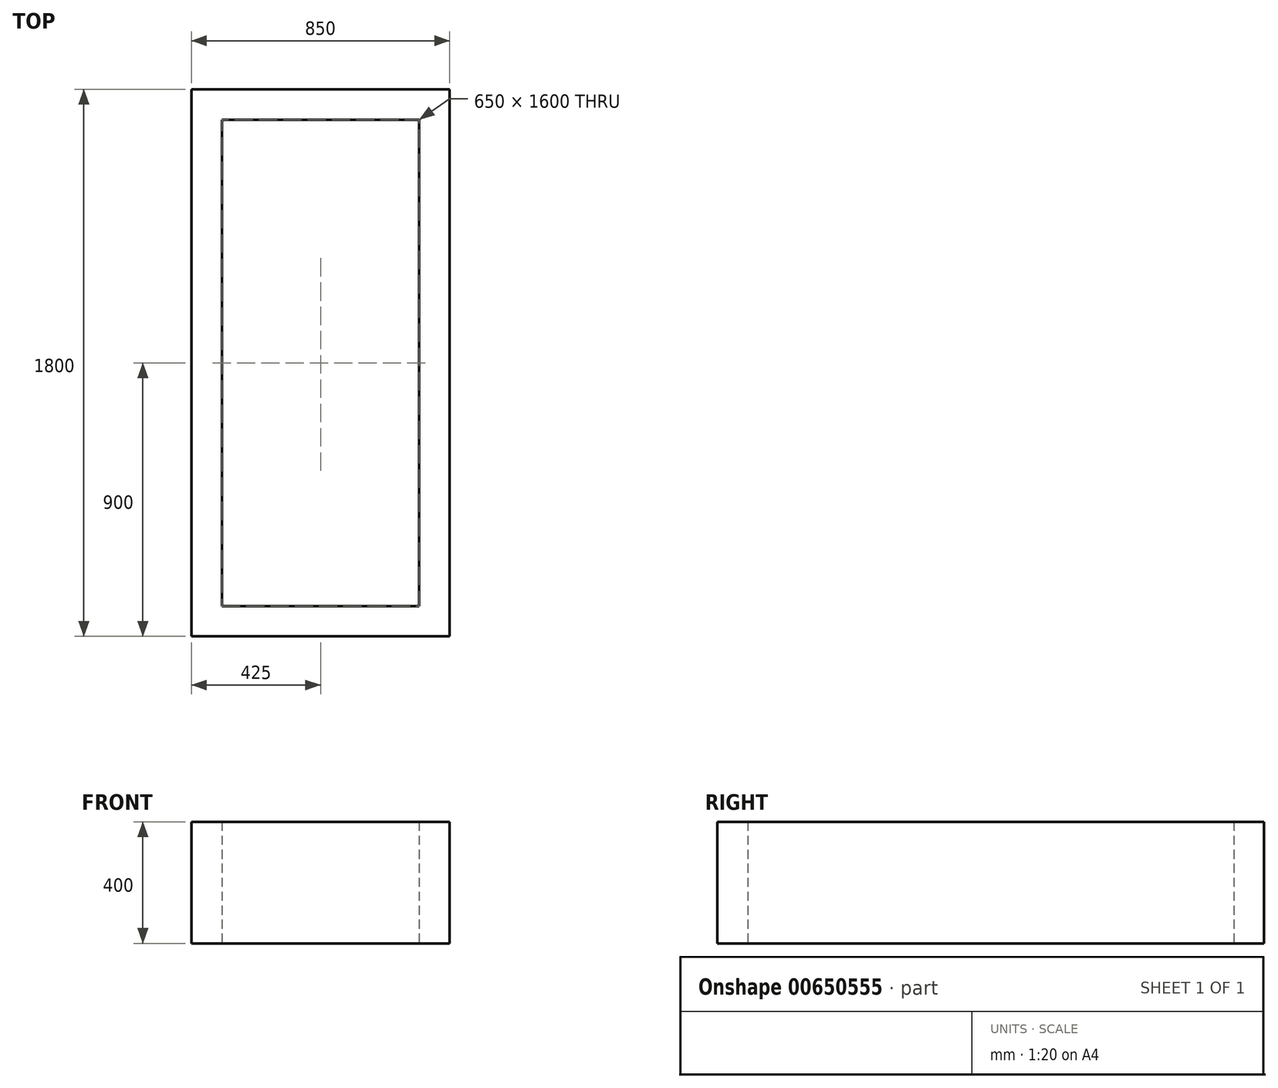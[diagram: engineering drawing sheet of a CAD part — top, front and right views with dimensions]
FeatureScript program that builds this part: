
annotation { "Feature Type Name" : "Feature", "Feature Type Description" : "" }
export const myFeature = defineFeature(function(context is Context, id is Id, definition is map)
    precondition{}
    {
        {
            var Q0;
            Q0=qCreatedBy(makeId("Top.planeOp"),FACE);
            var sketch = newSketch(context, id + "F0", { "sketchPlane" : qUnion([Q0])});
            skLineSegment(sketch, "E0.bottom", {"start": v(0, 0) * mm, "end": v(-850, 0) * mm});
            skLineSegment(sketch, "E0.top", {"start": v(0, 1800) * mm, "end": v(-850, 1800) * mm});
            skLineSegment(sketch, "E0.left", {"start": v(0, 0) * mm, "end": v(0, 1800) * mm});
            skLineSegment(sketch, "E0.right", {"start": v(-850, 0) * mm, "end": v(-850, 1800) * mm});
            skLineSegment(sketch, "E1.bottom", {"start": v(-750, 1700) * mm, "end": v(-100, 1700) * mm});
            skLineSegment(sketch, "E1.top", {"start": v(-750, 100) * mm, "end": v(-100, 100) * mm});
            skLineSegment(sketch, "E1.left", {"start": v(-750, 1700) * mm, "end": v(-750, 100) * mm});
            skLineSegment(sketch, "E1.right", {"start": v(-100, 1700) * mm, "end": v(-100, 100) * mm});
            skSolve(sketch);
        }
        {
            var Q0;
            Q0 = qSketchRegion(id + "F0", true);
            extrude(context, id + "F1", {"entities" : qUnion([Q0]), "depth" : 400 * mm, "offsetDistance" : 25 * mm});
        }
    });
